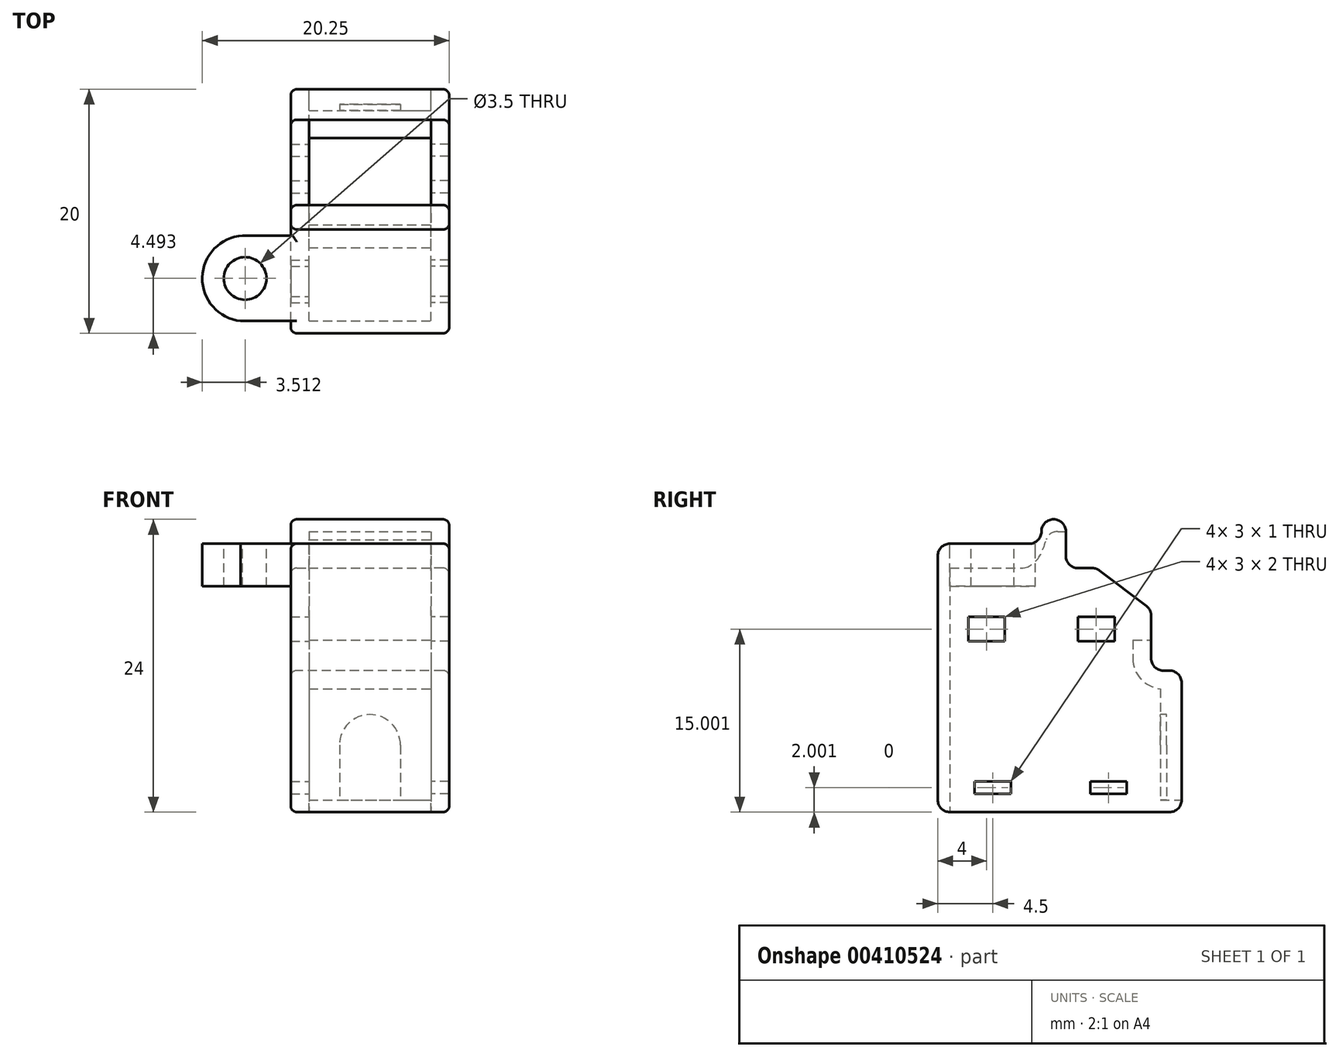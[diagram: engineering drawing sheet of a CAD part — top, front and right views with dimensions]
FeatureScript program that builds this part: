
annotation { "Feature Type Name" : "Feature", "Feature Type Description" : "" }
export const myFeature = defineFeature(function(context is Context, id is Id, definition is map)
    precondition{}
    {
        {
            var Q0;
            Q0=qCreatedBy(makeId("Right.planeOp"),FACE);
            var sketch = newSketch(context, id + "F0", { "sketchPlane" : qUnion([Q0])});
            skLineSegment(sketch, "E0.bottom", {"start": v(-10.5, 24) * mm, "end": v(-10.5, 24) * mm});
            skLineSegment(sketch, "E0.top", {"start": v(-19, 0) * mm, "end": v(-1, 0) * mm});
            skLineSegment(sketch, "E0.left", {"start": v(-20, 21) * mm, "end": v(-20, 1) * mm});
            skLineSegment(sketch, "E0.right", {"start": v(0, 10.6) * mm, "end": v(0, 1) * mm});
            skLineSegment(sketch, "E1.top", {"start": v(-7.34, 20) * mm, "end": v(-8.5, 20) * mm});
            skLineSegment(sketch, "E1.right", {"start": v(-9.5, 23) * mm, "end": v(-9.5, 21) * mm});
            skLineSegment(sketch, "E2.bottom", {"start": v(-1.5, 11.6) * mm, "end": v(-1, 11.6) * mm});
            skLineSegment(sketch, "E3", {"start": v(-6.73, 19.8) * mm, "end": v(-2.9, 16.9) * mm});
            skLineSegment(sketch, "E4.top", {"start": v(-19, 22) * mm, "end": v(-12.5, 22) * mm});
            skLineSegment(sketch, "E4.right", {"start": v(-11.5, 23) * mm, "end": v(-11.5, 23) * mm});
            skLineSegment(sketch, "E5.bottom", {"start": v(-17.5, 16) * mm, "end": v(-14.5, 16) * mm});
            skLineSegment(sketch, "E5.top", {"start": v(-17.5, 14) * mm, "end": v(-14.5, 14) * mm});
            skLineSegment(sketch, "E5.left", {"start": v(-17.5, 16) * mm, "end": v(-17.5, 14) * mm});
            skLineSegment(sketch, "E5.right", {"start": v(-14.5, 16) * mm, "end": v(-14.5, 14) * mm});
            skLineSegment(sketch, "E6.bottom", {"start": v(-8.5, 16) * mm, "end": v(-5.5, 16) * mm});
            skLineSegment(sketch, "E6.top", {"start": v(-8.5, 14) * mm, "end": v(-5.5, 14) * mm});
            skLineSegment(sketch, "E6.left", {"start": v(-8.5, 16) * mm, "end": v(-8.5, 14) * mm});
            skLineSegment(sketch, "E6.right", {"start": v(-5.5, 16) * mm, "end": v(-5.5, 14) * mm});
            skLineSegment(sketch, "E7.bottom", {"start": v(-17, 2.5) * mm, "end": v(-14, 2.5) * mm});
            skLineSegment(sketch, "E7.top", {"start": v(-17, 1.5) * mm, "end": v(-14, 1.5) * mm});
            skLineSegment(sketch, "E7.left", {"start": v(-17, 2.5) * mm, "end": v(-17, 1.5) * mm});
            skLineSegment(sketch, "E7.right", {"start": v(-14, 2.5) * mm, "end": v(-14, 1.5) * mm});
            skLineSegment(sketch, "E8.bottom", {"start": v(-7.5, 2.5) * mm, "end": v(-4.5, 2.5) * mm});
            skLineSegment(sketch, "E8.top", {"start": v(-7.5, 1.5) * mm, "end": v(-4.5, 1.5) * mm});
            skLineSegment(sketch, "E8.left", {"start": v(-7.5, 2.5) * mm, "end": v(-7.5, 1.5) * mm});
            skLineSegment(sketch, "E8.right", {"start": v(-4.5, 2.5) * mm, "end": v(-4.5, 1.5) * mm});
            skPoint(sketch, "E9", {"position": v(-2.5, 14.1) * mm});
            skLineSegment(sketch, "E10", {"start": v(-2.5, 16.1) * mm, "end": v(-2.5, 14.1) * mm});
            skLineSegment(sketch, "E11", {"start": v(-2.5, 14.1) * mm, "end": v(-2.5, 12.6) * mm});
            skPoint(sketch, "E12.visualSharp", {"position": v(-11.5, 24) * mm});
            skArc(sketch, "E12.filletArc", {"start": v(-10.5, 24) * mm, "mid": v(-11.2, 23.7) * mm, "end": v(-11.5, 23) * mm});
            skPoint(sketch, "E13.visualSharp", {"position": v(-11.5, 22) * mm});
            skArc(sketch, "E13.filletArc", {"start": v(-12.5, 22) * mm, "mid": v(-11.8, 22.3) * mm, "end": v(-11.5, 23) * mm});
            skPoint(sketch, "E14.visualSharp", {"position": v(-7, 20) * mm});
            skArc(sketch, "E14.filletArc", {"start": v(-6.73, 19.8) * mm, "mid": v(-7.02, 19.95) * mm, "end": v(-7.34, 20) * mm});
            skPoint(sketch, "E15.visualSharp", {"position": v(-2.5, 16.6) * mm});
            skArc(sketch, "E15.filletArc", {"start": v(-2.5, 16.1) * mm, "mid": v(-2.6, 16.55) * mm, "end": v(-2.9, 16.9) * mm});
            skPoint(sketch, "E16.visualSharp", {"position": v(-20, 22) * mm});
            skArc(sketch, "E16.filletArc", {"start": v(-19, 22) * mm, "mid": v(-19.7, 21.7) * mm, "end": v(-20, 21) * mm});
            skPoint(sketch, "E17.visualSharp", {"position": v(-9.5, 24) * mm});
            skArc(sketch, "E17.filletArc", {"start": v(-9.5, 23) * mm, "mid": v(-9.8, 23.7) * mm, "end": v(-10.5, 24) * mm});
            skPoint(sketch, "E18.visualSharp", {"position": v(-2.5, 11.6) * mm});
            skArc(sketch, "E18.filletArc", {"start": v(-2.5, 12.6) * mm, "mid": v(-2.2, 11.9) * mm, "end": v(-1.5, 11.6) * mm});
            skPoint(sketch, "E19.visualSharp", {"position": v(0, 11.6) * mm});
            skArc(sketch, "E19.filletArc", {"start": v(0, 10.6) * mm, "mid": v(-0.3, 11.3) * mm, "end": v(-1, 11.6) * mm});
            skPoint(sketch, "E20.visualSharp", {"position": v(-20, 0) * mm});
            skArc(sketch, "E20.filletArc", {"start": v(-20, 1) * mm, "mid": v(-19.7, 0.3) * mm, "end": v(-19, 0) * mm});
            skPoint(sketch, "E21.visualSharp", {"position": v(0, 0) * mm});
            skArc(sketch, "E21.filletArc", {"start": v(-1, 0) * mm, "mid": v(-0.3, 0.3) * mm, "end": v(0, 1) * mm});
            skLineSegment(sketch, "E22.0", {"start": v(-19, 20) * mm, "end": v(-19, 1) * mm});
            skLineSegment(sketch, "E22.1", {"start": v(-19, 20) * mm, "end": v(-13, 20) * mm});
            skLineSegment(sketch, "E23", {"start": v(-19, 1) * mm, "end": v(-19, 0) * mm});
            skPoint(sketch, "E24.visualSharp", {"position": v(-11, 23) * mm});
            skArc(sketch, "E24.filletArc", {"start": v(-10.17, 23) * mm, "mid": v(-10.75, 22.82) * mm, "end": v(-11.11, 22.33) * mm});
            skLineSegment(sketch, "E25", {"start": v(-10.17, 23) * mm, "end": v(-9.5, 23) * mm});
            skLineSegment(sketch, "E26.0", {"start": v(-1.75, 10.11) * mm, "end": v(-1.75, 1) * mm});
            skLineSegment(sketch, "E27.1", {"start": v(-4, 14.1) * mm, "end": v(-4, 12.6) * mm});
            skLineSegment(sketch, "E28", {"start": v(-4, 14.1) * mm, "end": v(-2.5, 14.1) * mm});
            skArc(sketch, "E29", {"start": v(-4, 12.6) * mm, "mid": v(-3.35, 10.92) * mm, "end": v(-1.75, 10.11) * mm});
            skLineSegment(sketch, "E30", {"start": v(-1.75, 1) * mm, "end": v(0, 1) * mm});
            skFitSpline(sketch, "E31", {"points": [v(-13, 20) * mm, v(-11.8, 20.78) * mm, v(-11.11, 22.33) * mm], "startDerivative": vector(3.1, 0.55) * mm, "endDerivative": vector(0.82, 3.1) * mm});
            skPoint(sketch, "E32.visualSharp", {"position": v(-9.5, 20) * mm});
            skArc(sketch, "E32.filletArc", {"start": v(-9.5, 21) * mm, "mid": v(-9.2, 20.3) * mm, "end": v(-8.5, 20) * mm});
            skSolve(sketch);
        }
        {
            var Q0;
            {var subQ0=sQuery(id+"F0.wireOp",EDGE,"E0.right");Q0=makeQuery(id+"F0.imprint","IMPRINT",FACE,{"disambiguationData":[TD([[makeQuery(id+"F0.imprint","IMPRINT",EDGE,{"derivedFrom":subQ0}),-1.0]])]});}
            var Q1;
            {var subQ1=sQuery(id+"F0.wireOp",EDGE,"E0.bottom");Q1=makeQuery(id+"F0.imprint","IMPRINT",FACE,{"disambiguationData":[TD([[makeQuery(id+"F0.imprint","IMPRINT",EDGE,{"derivedFrom":subQ1}),-1.0]])]});}
            var Q2;
            {var subQ1=sQuery(id+"F0.wireOp",EDGE,"E1.top");Q2=makeQuery(id+"F0.imprint","IMPRINT",FACE,{"disambiguationData":[TD([[makeQuery(id+"F0.imprint","IMPRINT",EDGE,{"derivedFrom":subQ1}),1.0]])]});}
            var Q3;
            Q3=makeQuery(id+"F0.imprint","IMPRINT",FACE,{"disambiguationData":[TD([[makeQuery(id+"F0.imprint","IMPRINT",EDGE,{"derivedFrom":sQuery(id+"F0.wireOp",EDGE,"E6.bottom")}),-1.0]])]});
            var Q4;
            Q4=makeQuery(id+"F0.imprint","IMPRINT",FACE,{"disambiguationData":[TD([[makeQuery(id+"F0.imprint","IMPRINT",EDGE,{"derivedFrom":sQuery(id+"F0.wireOp",EDGE,"E8.bottom")}),-1.0]])]});
            var Q5;
            Q5=makeQuery(id+"F0.imprint","IMPRINT",FACE,{"disambiguationData":[TD([[makeQuery(id+"F0.imprint","IMPRINT",EDGE,{"derivedFrom":sQuery(id+"F0.wireOp",EDGE,"E7.bottom")}),-1.0]])]});
            var Q6;
            Q6=makeQuery(id+"F0.imprint","IMPRINT",FACE,{"disambiguationData":[TD([[makeQuery(id+"F0.imprint","IMPRINT",EDGE,{"derivedFrom":sQuery(id+"F0.wireOp",EDGE,"E5.bottom")}),-1.0]])]});
            var Q7;
            Q7=makeQuery(id+"F0.imprint","IMPRINT",FACE,{"disambiguationData":[TD([[makeQuery(id+"F0.imprint","IMPRINT",EDGE,{"derivedFrom":sQuery(id+"F0.wireOp",EDGE,"E0.left")}),1.0]])]});
            extrude(context, id + "F1", {"entities" : qUnion([Q0, Q1, Q2, Q3, Q4, Q5, Q6, Q7]), "depth" : 1.5 * mm});
        }
        {
            var Q0;
            Q0=makeQuery(id+"F0.imprint","IMPRINT",FACE,{"disambiguationData":[TD([[makeQuery(id+"F0.imprint","IMPRINT",EDGE,{"derivedFrom":sQuery(id+"F0.wireOp",EDGE,"E6.bottom")}),-1.0]])]});
            var Q1;
            Q1=makeQuery(id+"F0.imprint","IMPRINT",FACE,{"disambiguationData":[TD([[makeQuery(id+"F0.imprint","IMPRINT",EDGE,{"derivedFrom":sQuery(id+"F0.wireOp",EDGE,"E5.bottom")}),-1.0]])]});
            var Q2;
            Q2=makeQuery(id+"F0.imprint","IMPRINT",FACE,{"disambiguationData":[TD([[makeQuery(id+"F0.imprint","IMPRINT",EDGE,{"derivedFrom":sQuery(id+"F0.wireOp",EDGE,"E7.bottom")}),-1.0]])]});
            var Q3;
            Q3=makeQuery(id+"F0.imprint","IMPRINT",FACE,{"disambiguationData":[TD([[makeQuery(id+"F0.imprint","IMPRINT",EDGE,{"derivedFrom":sQuery(id+"F0.wireOp",EDGE,"E8.bottom")}),-1.0]])]});
            extrude(context, id + "F2", {"entities" : qUnion([Q0, Q1, Q2, Q3]), "operationType" : NewBodyOperationType.REMOVE, "endBound" : BoundingType.THROUGH_ALL, "depth" : 25 * mm});
        }
        {
            var Q0;
            Q0=makeQuery(id+"F0.imprint","IMPRINT",FACE,{"disambiguationData":[TD([[makeQuery(id+"F0.imprint","IMPRINT",EDGE,{"derivedFrom":sQuery(id+"F0.wireOp",EDGE,"E0.left")}),1.0]])]});
            var Q1;
            Q1=makeQuery(id+"F0.imprint","IMPRINT",FACE,{"disambiguationData":[TD([[makeQuery(id+"F0.imprint","IMPRINT",EDGE,{"derivedFrom":sQuery(id+"F0.wireOp",EDGE,"E0.right")}),-1.0]])]});
            extrude(context, id + "F3", {"entities" : qUnion([Q0, Q1]), "operationType" : NewBodyOperationType.ADD, "oppositeDirection" : true, "depth" : 5 * mm});
        }
        {
            var Q0;
            Q0=makeQuery(id+"F1.opExtrude","SWEPT_BODY",BODY,{"disambiguationData":[OSD([sQuery(id+"F0.wireOp",EDGE,"E0.bottom"),sQuery(id+"F0.wireOp",EDGE,"E0.top"),sQuery(id+"F0.wireOp",EDGE,"E0.left"),sQuery(id+"F0.wireOp",EDGE,"E0.right"),sQuery(id+"F0.wireOp",EDGE,"E1.top"),sQuery(id+"F0.wireOp",EDGE,"E1.right"),sQuery(id+"F0.wireOp",EDGE,"E2.bottom"),sQuery(id+"F0.wireOp",EDGE,"E3"),sQuery(id+"F0.wireOp",EDGE,"E4.top"),sQuery(id+"F0.wireOp",EDGE,"E4.right"),sQuery(id+"F0.wireOp",EDGE,"E10"),sQuery(id+"F0.wireOp",EDGE,"E11")])]});
            var Q1;
            Q1=sQuery(id+"F0.wireOp",VERTEX,"E0.right.end");
            var Q2;
            Q2=makeQuery(id+"F3.opExtrude","CAP_VERTEX",VERTEX,{"disambiguationData":[OSD([sQuery(id+"F0.wireOp",EDGE,"E0.top"),sQuery(id+"F0.wireOp",EDGE,"E0.right")])],"isStart":false});
            transform(context, id + "F4", {"entities" : qUnion([Q0]), "transformType" : TransformType.TRANSLATION_ENTITY, "oppositeDirectionEntity" : true, "transformLine" : qUnion([Q1, Q2]), "makeCopy" : false});
        }
        {
            var Q0;
            Q0=makeQuery(id+"F1.opExtrude","SWEPT_BODY",BODY,{"disambiguationData":[OSD([sQuery(id+"F0.wireOp",EDGE,"E0.bottom"),sQuery(id+"F0.wireOp",EDGE,"E0.top"),sQuery(id+"F0.wireOp",EDGE,"E0.left"),sQuery(id+"F0.wireOp",EDGE,"E0.right"),sQuery(id+"F0.wireOp",EDGE,"E1.top"),sQuery(id+"F0.wireOp",EDGE,"E1.right"),sQuery(id+"F0.wireOp",EDGE,"E2.bottom"),sQuery(id+"F0.wireOp",EDGE,"E3"),sQuery(id+"F0.wireOp",EDGE,"E4.top"),sQuery(id+"F0.wireOp",EDGE,"E4.right"),sQuery(id+"F0.wireOp",EDGE,"E10"),sQuery(id+"F0.wireOp",EDGE,"E11")])]});
            var Q1;
            Q1=qCreatedBy(makeId("Right.planeOp"),FACE);
            mirror(context, id + "F5", {"operationType" : NewBodyOperationType.ADD, "entities" : qUnion([Q0]), "mirrorPlane" : qUnion([Q1])});
        }
        {
            var Q0;
            Q0=makeQuery(id+"F1.opExtrude","CAP_EDGE",EDGE,{"disambiguationData":[OSD([sQuery(id+"F0.wireOp",EDGE,"E0.left")])],"isStart":false});
            var Q1;
            Q1=makeQuery(id+"F5.opPattern","COPY",EDGE,{"derivedFrom":makeQuery(id+"F1.opExtrude","CAP_EDGE",EDGE,{"disambiguationData":[OSD([sQuery(id+"F0.wireOp",EDGE,"E16.filletArc")])],"isStart":false}),"instanceName":"1"});
            fillet(context, id + "F6", {"entities" : qUnion([Q0, Q1]), "radius" : .5 * mm, "tangentPropagation" : true, "allowEdgeOverflow" : false});
        }
        {
            var Q0;
            {var subQ0=sQuery(id+"F0.wireOp",EDGE,"E0.left");var subQ1=makeQuery(id+"F3.boolean.opBoolean","MERGE",FACE,{"derivedFrom":[makeQuery(id+"F1.opExtrude","SWEPT_FACE",FACE,{"disambiguationData":[OSD([subQ0])]}),makeQuery(id+"F3.opExtrude","SWEPT_FACE",FACE,{"disambiguationData":[OSD([subQ0])]})]});Q0=makeQuery(id+"F5.boolean.opBoolean","MERGE",FACE,{"derivedFrom":[subQ1,makeQuery(id+"F5.opPattern","COPY",FACE,{"derivedFrom":subQ1,"instanceName":"1"})]});}
            var sketch = newSketch(context, id + "F7", { "sketchPlane" : qUnion([Q0])});
            skArc(sketch, "E33", {"start": v(4, -4.1) * mm, "mid": v(0, -0.1) * mm, "end": v(-4, -4.1) * mm});
            skLineSegment(sketch, "E34.top", {"start": v(-4, -9.6) * mm, "end": v(4, -9.6) * mm});
            skLineSegment(sketch, "E34.left", {"start": v(-4, -4.1) * mm, "end": v(-4, -9.6) * mm});
            skLineSegment(sketch, "E34.right", {"start": v(4, -4.1) * mm, "end": v(4, -9.6) * mm});
            skSolve(sketch);
        }
        {
            var Q0;
            {var subQ0=sQuery(id+"F7.wireOp",EDGE,"E34.top");Q0=makeQuery(id+"F7.imprint","IMPRINT",FACE,{"disambiguationData":[TD([[makeQuery(id+"F7.imprint","IMPRINT",EDGE,{"derivedFrom":subQ0}),1.0]])]});}
            var Q1;
            {var subQ0=sQuery(id+"F7.wireOp",EDGE,"E33");Q1=makeQuery(id+"F7.imprint","IMPRINT",FACE,{"disambiguationData":[TD([[makeQuery(id+"F7.imprint","IMPRINT",EDGE,{"derivedFrom":subQ0}),1.0]])]});}
            extrude(context, id + "F8", {"entities" : qUnion([Q0, Q1]), "operationType" : NewBodyOperationType.REMOVE, "endBound" : BoundingType.UP_TO_NEXT, "oppositeDirection" : true, "depth" : 18.75 * mm});
        }
        {
            var Q0;
            {var subQ0=makeQuery(id+"F3.opExtrude","SWEPT_FACE",FACE,{"disambiguationData":[OSD([sQuery(id+"F0.wireOp",EDGE,"E26.0")])]});Q0=makeQuery(id+"F5.boolean.opBoolean","MERGE",FACE,{"derivedFrom":[subQ0,makeQuery(id+"F5.opPattern","COPY",FACE,{"derivedFrom":subQ0,"instanceName":"1"})]});}
            var sketch = newSketch(context, id + "F9", { "sketchPlane" : qUnion([Q0])});
            skArc(sketch, "E35", {"start": v(2.5, -4.1) * mm, "mid": v(0, -1.6) * mm, "end": v(-2.5, -4.1) * mm});
            skLineSegment(sketch, "E36.top", {"start": v(-2.5, -8.6) * mm, "end": v(2.5, -8.6) * mm});
            skLineSegment(sketch, "E36.left", {"start": v(-2.5, -4.1) * mm, "end": v(-2.5, -8.6) * mm});
            skLineSegment(sketch, "E36.right", {"start": v(2.5, -4.1) * mm, "end": v(2.5, -8.6) * mm});
            skSolve(sketch);
        }
        {
            var Q0;
            Q0=makeQuery(id+"F9.imprint","IMPRINT",FACE,{"disambiguationData":[TD([[makeQuery(id+"F9.imprint","IMPRINT",EDGE,{"derivedFrom":sQuery(id+"F9.wireOp",EDGE,"E35")}),1.0]])]});
            extrude(context, id + "F10", {"entities" : qUnion([Q0]), "operationType" : NewBodyOperationType.REMOVE, "oppositeDirection" : true, "depth" : .5 * mm});
        }
        {
            var Q0;
            Q0=makeQuery(id+"F5.opPattern","COPY",FACE,{"derivedFrom":makeQuery(id+"F1.opExtrude","CAP_FACE",FACE,{"disambiguationData":[OSD([sQuery(id+"F0.wireOp",EDGE,"E0.bottom"),sQuery(id+"F0.wireOp",EDGE,"E0.top"),sQuery(id+"F0.wireOp",EDGE,"E0.left"),sQuery(id+"F0.wireOp",EDGE,"E0.right"),sQuery(id+"F0.wireOp",EDGE,"E1.top"),sQuery(id+"F0.wireOp",EDGE,"E1.right"),sQuery(id+"F0.wireOp",EDGE,"E2.bottom"),sQuery(id+"F0.wireOp",EDGE,"E3"),sQuery(id+"F0.wireOp",EDGE,"E4.top"),sQuery(id+"F0.wireOp",EDGE,"E10"),sQuery(id+"F0.wireOp",EDGE,"E11"),sQuery(id+"F0.wireOp",EDGE,"E12.filletArc"),sQuery(id+"F0.wireOp",EDGE,"E13.filletArc"),sQuery(id+"F0.wireOp",EDGE,"E14.filletArc"),sQuery(id+"F0.wireOp",EDGE,"E15.filletArc"),sQuery(id+"F0.wireOp",EDGE,"E16.filletArc"),sQuery(id+"F0.wireOp",EDGE,"E17.filletArc"),sQuery(id+"F0.wireOp",EDGE,"E18.filletArc"),sQuery(id+"F0.wireOp",EDGE,"E19.filletArc"),sQuery(id+"F0.wireOp",EDGE,"E20.filletArc"),sQuery(id+"F0.wireOp",EDGE,"E21.filletArc")])],"isStart":false}),"instanceName":"1"});
            var sketch = newSketch(context, id + "F11", { "sketchPlane" : qUnion([Q0])});
            skLineSegment(sketch, "E37.bottom", {"start": v(12, 12.4) * mm, "end": v(19, 12.4) * mm});
            skLineSegment(sketch, "E37.top", {"start": v(12, 8.9) * mm, "end": v(19, 8.9) * mm});
            skLineSegment(sketch, "E37.left", {"start": v(12, 12.4) * mm, "end": v(12, 8.9) * mm});
            skLineSegment(sketch, "E37.right", {"start": v(19, 12.4) * mm, "end": v(19, 8.9) * mm});
            skSolve(sketch);
        }
        {
            var Q0;
            {var subQ6=sQuery(id+"F11.wireOp",EDGE,"E37.bottom");Q0=makeQuery(id+"F11.imprint","IMPRINT",FACE,{"disambiguationData":[TD([[makeQuery(id+"F11.imprint","IMPRINT",EDGE,{"derivedFrom":subQ6}),-1.0]])]});}
            var Q1;
            {var subQ6=sQuery(id+"F11.wireOp",EDGE,"E37.top");Q1=makeQuery(id+"F11.imprint","IMPRINT",FACE,{"disambiguationData":[TD([[makeQuery(id+"F11.imprint","IMPRINT",EDGE,{"derivedFrom":subQ6}),1.0]])]});}
            extrude(context, id + "F12", {"entities" : qUnion([Q0, Q1]), "operationType" : NewBodyOperationType.ADD, "depth" : 7.25 * mm, "hasSecondDirection" : true, "secondDirectionOppositeDirection" : true, "secondDirectionDepth" : .5 * mm});
        }
        {
            var Q0;
            Q0=makeQuery(id+"F12.opExtrude","SWEPT_FACE",FACE,{"disambiguationData":[OSD([sQuery(id+"F11.wireOp",EDGE,"E37.bottom")])]});
            var sketch = newSketch(context, id + "F13", { "sketchPlane" : qUnion([Q0])});
            skCircle(sketch, "E38", {"center": v(-10.24, -15.5) * mm, "radius": 3.51 * mm});
            skCircle(sketch, "E39", {"center": v(-10.24, -15.5) * mm, "radius": 1.75 * mm});
            skSolve(sketch);
        }
        {
            var Q0;
            Q0=makeQuery(id+"F13.imprint","IMPRINT",FACE,{"disambiguationData":[TD([[makeQuery(id+"F13.imprint","IMPRINT",EDGE,{"derivedFrom":sQuery(id+"F13.wireOp",EDGE,"E39")}),1.0]])]});
            var Q1;
            {var subQ0=sQuery(id+"F13.wireOp",EDGE,"E38");var subQ1=sQuery(id+"F11.wireOp",EDGE,"E37.bottom");var subQ2=makeQuery(id+"F12.opExtrude","CAP_EDGE",EDGE,{"disambiguationData":[OSD([subQ1])],"isStart":false});var subQ3=makeQuery(id+"F13.imprint","INTERSECT",VERTEX,{"derivedFrom":[subQ2,subQ0]});Q1=makeQuery(id+"F13.imprint","IMPRINT",FACE,{"disambiguationData":[TD([[makeQuery(id+"F13.imprint","IMPRINT",EDGE,{"disambiguationData":[TD([[subQ3,-1.0]])],"derivedFrom":subQ0}),-1.0]])]});}
            var Q2;
            {var subQ0=sQuery(id+"F13.wireOp",EDGE,"E38");var subQ1=sQuery(id+"F11.wireOp",EDGE,"E37.bottom");var subQ4=makeQuery(id+"F12.opExtrude","CAP_EDGE",EDGE,{"disambiguationData":[OSD([subQ1])],"isStart":false});var subQ5=makeQuery(id+"F13.imprint","INTERSECT",VERTEX,{"derivedFrom":[subQ4,subQ0]});Q2=makeQuery(id+"F13.imprint","IMPRINT",FACE,{"disambiguationData":[TD([[makeQuery(id+"F13.imprint","IMPRINT",EDGE,{"disambiguationData":[TD([[subQ5,1.0]])],"derivedFrom":subQ0}),-1.0]])]});}
            extrude(context, id + "F14", {"entities" : qUnion([Q0, Q1, Q2]), "operationType" : NewBodyOperationType.REMOVE, "endBound" : BoundingType.THROUGH_ALL, "oppositeDirection" : true, "depth" : 25 * mm});
        }
    });
